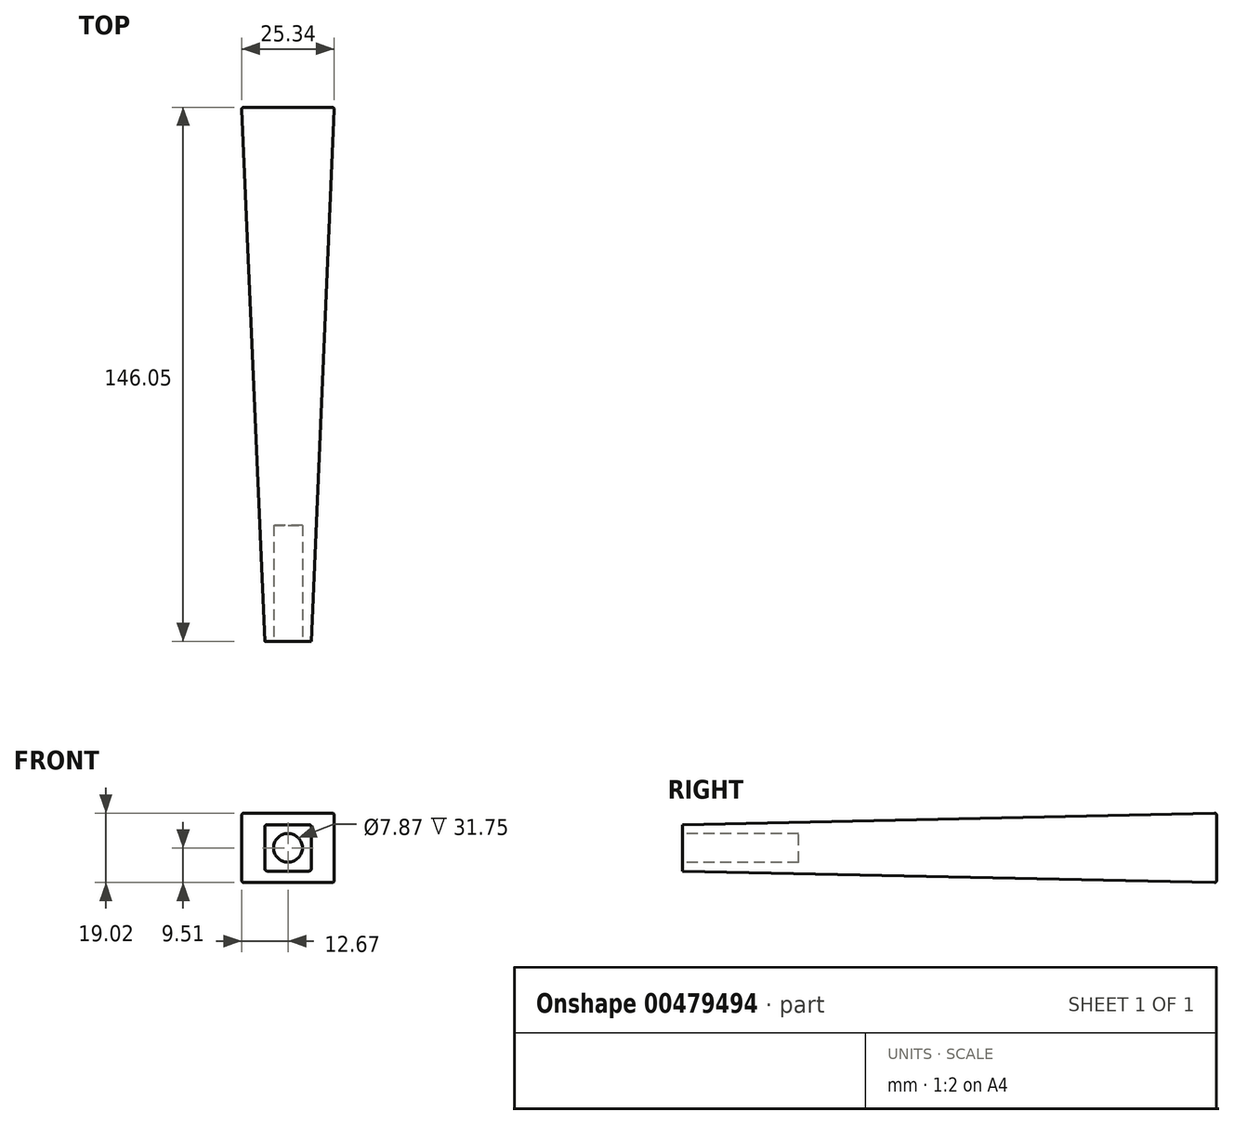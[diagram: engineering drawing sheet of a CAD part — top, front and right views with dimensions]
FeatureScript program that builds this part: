
annotation { "Feature Type Name" : "Feature", "Feature Type Description" : "" }
export const myFeature = defineFeature(function(context is Context, id is Id, definition is map)
    precondition{}
    {
        {
            var Q0;
            Q0=qCreatedBy(makeId("Front.planeOp"),FACE);
            var sketch = newSketch(context, id + "F0", { "sketchPlane" : qUnion([Q0])});
            skLineSegment(sketch, "E0.bottom", {"start": v(-12.7, 9.53) * mm, "end": v(12.7, 9.53) * mm});
            skLineSegment(sketch, "E0.top", {"start": v(-12.7, -9.53) * mm, "end": v(12.7, -9.53) * mm});
            skLineSegment(sketch, "E0.left", {"start": v(-12.7, 9.53) * mm, "end": v(-12.7, -9.53) * mm});
            skLineSegment(sketch, "E0.right", {"start": v(12.7, 9.53) * mm, "end": v(12.7, -9.53) * mm});
            skSolve(sketch);
        }
        {
            var Q0;
            Q0=makeQuery(id+"F0.imprint","IMPRINT",FACE,{"disambiguationData":[TD([[makeQuery(id+"F0.imprint","IMPRINT",EDGE,{"derivedFrom":sQuery(id+"F0.wireOp",EDGE,"E0.bottom")}),-1.0]])]});
            extrude(context, id + "F1", {"entities" : qUnion([Q0]), "depth" : 146.05 * mm});
        }
        {
            var Q0;
            Q0=makeQuery(id+"F1.opExtrude","CAP_FACE",FACE,{"disambiguationData":[OSD([sQuery(id+"F0.wireOp",EDGE,"E0.bottom"),sQuery(id+"F0.wireOp",EDGE,"E0.top"),sQuery(id+"F0.wireOp",EDGE,"E0.left"),sQuery(id+"F0.wireOp",EDGE,"E0.right")])],"isStart":false});
            var sketch = newSketch(context, id + "F2", { "sketchPlane" : qUnion([Q0])});
            skLineSegment(sketch, "E1", {"start": v(-12.7, 9.53) * mm, "end": v(12.7, -9.53) * mm});
            skLineSegment(sketch, "E2", {"start": v(-12.7, -9.53) * mm, "end": v(12.7, 9.53) * mm});
            skLineSegment(sketch, "E3.bottom", {"start": v(-6.16, 6.06) * mm, "end": v(6.54, 6.06) * mm});
            skLineSegment(sketch, "E3.top", {"start": v(-6.16, -6.64) * mm, "end": v(6.54, -6.64) * mm});
            skLineSegment(sketch, "E3.left", {"start": v(-6.16, 6.06) * mm, "end": v(-6.16, -6.64) * mm});
            skLineSegment(sketch, "E3.right", {"start": v(6.54, 6.06) * mm, "end": v(6.54, -6.64) * mm});
            skLineSegment(sketch, "E4", {"start": v(12.7, 0) * mm, "end": v(-12.7, 0) * mm});
            skSolve(sketch);
        }
        {
            var Q0;
            Q0=makeQuery(id+"F1.opExtrude","SWEPT_FACE",FACE,{"disambiguationData":[OSD([sQuery(id+"F0.wireOp",EDGE,"E0.left")])]});
            var sketch = newSketch(context, id + "F3", { "sketchPlane" : qUnion([Q0])});
            skLineSegment(sketch, "E5", {"start": v(0, 9.53) * mm, "end": v(146.05, 6.35) * mm});
            skLineSegment(sketch, "E6", {"start": v(146.05, 6.35) * mm, "end": v(146.05, 9.53) * mm});
            skLineSegment(sketch, "E7", {"start": v(146.05, 9.53) * mm, "end": v(0, 9.53) * mm});
            skSolve(sketch);
        }
        {
            var Q0;
            Q0=makeQuery(id+"F3.imprint","IMPRINT",FACE,{"disambiguationData":[TD([[makeQuery(id+"F3.imprint","IMPRINT",EDGE,{"derivedFrom":sQuery(id+"F3.wireOp",EDGE,"E5")}),1.0]])]});
            extrude(context, id + "F4", {"entities" : qUnion([Q0]), "operationType" : NewBodyOperationType.REMOVE, "oppositeDirection" : true, "depth" : 25.4 * mm});
        }
        {
            var Q0;
            Q0=makeQuery(id+"F1.opExtrude","SWEPT_FACE",FACE,{"disambiguationData":[OSD([sQuery(id+"F0.wireOp",EDGE,"E0.left")])]});
            var sketch = newSketch(context, id + "F5", { "sketchPlane" : qUnion([Q0])});
            skLineSegment(sketch, "E8", {"start": v(0, -9.53) * mm, "end": v(146.05, -6.35) * mm});
            skLineSegment(sketch, "E9", {"start": v(146.05, -6.35) * mm, "end": v(146.05, -9.53) * mm});
            skLineSegment(sketch, "E10", {"start": v(146.05, -9.53) * mm, "end": v(0, -9.53) * mm});
            skSolve(sketch);
        }
        {
            var Q0;
            Q0=makeQuery(id+"F5.imprint","IMPRINT",FACE,{"disambiguationData":[TD([[makeQuery(id+"F5.imprint","IMPRINT",EDGE,{"derivedFrom":sQuery(id+"F5.wireOp",EDGE,"E8")}),-1.0]])]});
            extrude(context, id + "F6", {"entities" : qUnion([Q0]), "operationType" : NewBodyOperationType.REMOVE, "oppositeDirection" : true, "depth" : 25.4 * mm});
        }
        {
            var Q0;
            Q0=qCreatedBy(makeId("Top.planeOp"),FACE);
            var sketch = newSketch(context, id + "F7", { "sketchPlane" : qUnion([Q0])});
            skLineSegment(sketch, "E11", {"start": v(12.7, -146.05) * mm, "end": v(-12.7, -146.05) * mm});
            skLineSegment(sketch, "E12", {"start": v(-12.7, 0) * mm, "end": v(-6.35, -146.05) * mm});
            skLineSegment(sketch, "E13", {"start": v(12.7, 0) * mm, "end": v(6.35, -146.05) * mm});
            skLineSegment(sketch, "E14", {"start": v(12.7, 0) * mm, "end": v(12.7, -146.05) * mm});
            skLineSegment(sketch, "E15", {"start": v(-12.7, 0) * mm, "end": v(-12.7, -146.05) * mm});
            skSolve(sketch);
        }
        {
            var Q0;
            Q0 = qSketchRegion(id + "F7", true);
            extrude(context, id + "F8", {"entities" : qUnion([Q0]), "operationType" : NewBodyOperationType.REMOVE, "endBound" : BoundingType.SYMMETRIC, "oppositeDirection" : true, "depth" : 25.4 * mm});
        }
        {
            var Q0;
            Q0=makeQuery(id+"F8.boolean.opBoolean","INTERSECT",EDGE,{"derivedFrom":[makeQuery(id+"F4.boolean.opBoolean","COPY",FACE,{"derivedFrom":makeQuery(id+"F4.opExtrude","SWEPT_FACE",FACE,{"disambiguationData":[OSD([sQuery(id+"F3.wireOp",EDGE,"E5")])]})}),makeQuery(id+"F8.opExtrude","SWEPT_FACE",FACE,{"disambiguationData":[OSD([sQuery(id+"F7.wireOp",EDGE,"E13")])]})]});
            var Q1;
            Q1=makeQuery(id+"F4.boolean.opBoolean","COPY",EDGE,{"derivedFrom":makeQuery(id+"F4.opExtrude","SWEPT_EDGE",EDGE,{"disambiguationData":[OSD([sQuery(id+"F0.wireOp",EDGE,"E0.left"),sQuery(id+"F3.wireOp",EDGE,"E5"),sQuery(id+"F3.wireOp",EDGE,"E6")])]})});
            var Q2;
            Q2=makeQuery(id+"F8.boolean.opBoolean","COPY",EDGE,{"derivedFrom":makeQuery(id+"F8.opExtrude","SWEPT_EDGE",EDGE,{"disambiguationData":[OSD([sQuery(id+"F7.wireOp",EDGE,"E11"),sQuery(id+"F7.wireOp",EDGE,"E13")])]})});
            var Q3;
            Q3=makeQuery(id+"F6.boolean.opBoolean","COPY",EDGE,{"derivedFrom":makeQuery(id+"F6.opExtrude","SWEPT_EDGE",EDGE,{"disambiguationData":[OSD([sQuery(id+"F0.wireOp",EDGE,"E0.left"),sQuery(id+"F5.wireOp",EDGE,"E8"),sQuery(id+"F5.wireOp",EDGE,"E9")])]})});
            var Q4;
            Q4=makeQuery(id+"F8.boolean.opBoolean","COPY",EDGE,{"derivedFrom":makeQuery(id+"F8.opExtrude","SWEPT_EDGE",EDGE,{"disambiguationData":[OSD([sQuery(id+"F7.wireOp",EDGE,"E11"),sQuery(id+"F7.wireOp",EDGE,"E12")])]})});
            var Q5;
            Q5=makeQuery(id+"F8.boolean.opBoolean","INTERSECT",EDGE,{"derivedFrom":[makeQuery(id+"F4.boolean.opBoolean","COPY",FACE,{"derivedFrom":makeQuery(id+"F4.opExtrude","SWEPT_FACE",FACE,{"disambiguationData":[OSD([sQuery(id+"F3.wireOp",EDGE,"E5")])]})}),makeQuery(id+"F8.opExtrude","SWEPT_FACE",FACE,{"disambiguationData":[OSD([sQuery(id+"F7.wireOp",EDGE,"E12")])]})]});
            var Q6;
            Q6=makeQuery(id+"F8.boolean.opBoolean","INTERSECT",EDGE,{"derivedFrom":[makeQuery(id+"F6.boolean.opBoolean","COPY",FACE,{"derivedFrom":makeQuery(id+"F6.opExtrude","SWEPT_FACE",FACE,{"disambiguationData":[OSD([sQuery(id+"F5.wireOp",EDGE,"E8")])]})}),makeQuery(id+"F8.opExtrude","SWEPT_FACE",FACE,{"disambiguationData":[OSD([sQuery(id+"F7.wireOp",EDGE,"E12")])]})]});
            var Q7;
            Q7=makeQuery(id+"F8.boolean.opBoolean","MERGE",EDGE,{"derivedFrom":[makeQuery(id+"F1.opExtrude","CAP_EDGE",EDGE,{"disambiguationData":[OSD([sQuery(id+"F0.wireOp",EDGE,"E0.right")])],"isStart":true}),makeQuery(id+"F8.opExtrude","SWEPT_EDGE",EDGE,{"disambiguationData":[OSD([sQuery(id+"F7.wireOp",EDGE,"E13"),sQuery(id+"F7.wireOp",EDGE,"E14")])]})]});
            var Q8;
            Q8=makeQuery(id+"F4.boolean.opBoolean","MERGE",EDGE,{"derivedFrom":[makeQuery(id+"F1.opExtrude","CAP_EDGE",EDGE,{"disambiguationData":[OSD([sQuery(id+"F0.wireOp",EDGE,"E0.bottom")])],"isStart":true}),makeQuery(id+"F4.opExtrude","SWEPT_EDGE",EDGE,{"disambiguationData":[OSD([sQuery(id+"F0.wireOp",EDGE,"E0.left"),sQuery(id+"F3.wireOp",EDGE,"E5"),sQuery(id+"F3.wireOp",EDGE,"E7")])]})]});
            var Q9;
            Q9=makeQuery(id+"F8.boolean.opBoolean","MERGE",EDGE,{"derivedFrom":[makeQuery(id+"F1.opExtrude","CAP_EDGE",EDGE,{"disambiguationData":[OSD([sQuery(id+"F0.wireOp",EDGE,"E0.left")])],"isStart":true}),makeQuery(id+"F8.opExtrude","SWEPT_EDGE",EDGE,{"disambiguationData":[OSD([sQuery(id+"F7.wireOp",EDGE,"E12"),sQuery(id+"F7.wireOp",EDGE,"E15")])]})]});
            var Q10;
            Q10=makeQuery(id+"F6.boolean.opBoolean","MERGE",EDGE,{"derivedFrom":[makeQuery(id+"F1.opExtrude","CAP_EDGE",EDGE,{"disambiguationData":[OSD([sQuery(id+"F0.wireOp",EDGE,"E0.top")])],"isStart":true}),makeQuery(id+"F6.opExtrude","SWEPT_EDGE",EDGE,{"disambiguationData":[OSD([sQuery(id+"F0.wireOp",EDGE,"E0.left"),sQuery(id+"F5.wireOp",EDGE,"E8"),sQuery(id+"F5.wireOp",EDGE,"E10")])]})]});
            var Q11;
            Q11=makeQuery(id+"F8.boolean.opBoolean","INTERSECT",EDGE,{"derivedFrom":[makeQuery(id+"F6.boolean.opBoolean","COPY",FACE,{"derivedFrom":makeQuery(id+"F6.opExtrude","SWEPT_FACE",FACE,{"disambiguationData":[OSD([sQuery(id+"F5.wireOp",EDGE,"E8")])]})}),makeQuery(id+"F8.opExtrude","SWEPT_FACE",FACE,{"disambiguationData":[OSD([sQuery(id+"F7.wireOp",EDGE,"E13")])]})]});
            fillet(context, id + "F9", {"entities" : qUnion([Q0, Q1, Q2, Q3, Q4, Q5, Q6, Q7, Q8, Q9, Q10, Q11]), "radius" : 0.64 * mm, "tangentPropagation" : true, "allowEdgeOverflow" : false});
        }
        {
            var Q0;
            Q0=makeQuery(id+"F1.opExtrude","CAP_FACE",FACE,{"disambiguationData":[OSD([sQuery(id+"F0.wireOp",EDGE,"E0.bottom"),sQuery(id+"F0.wireOp",EDGE,"E0.top"),sQuery(id+"F0.wireOp",EDGE,"E0.left"),sQuery(id+"F0.wireOp",EDGE,"E0.right")])],"isStart":false});
            var sketch = newSketch(context, id + "F10", { "sketchPlane" : qUnion([Q0])});
            skCircle(sketch, "E16", {"center": v(0, 0) * mm, "radius": 3.94 * mm});
            skSolve(sketch);
        }
        {
            var Q0;
            Q0=makeQuery(id+"F10.imprint","IMPRINT",FACE,{"disambiguationData":[TD([[makeQuery(id+"F10.imprint","IMPRINT",EDGE,{"derivedFrom":sQuery(id+"F10.wireOp",EDGE,"E16")}),1.0]])]});
            extrude(context, id + "F11", {"entities" : qUnion([Q0]), "operationType" : NewBodyOperationType.REMOVE, "oppositeDirection" : true, "depth" : 31.75 * mm});
        }
    });
